# Revit family: Asma klozet için Geberit Duofix elemanı, 112 cm, Alpha 12 cm gömme rezervuar ile, 6_3 litre_PRO_1779723
name_source: partatom
category: Plumbing Fixtures
units: mm (PartAtom-declared; Revit-internal decimal feet)

## family parameters
Always vertical = Yes
Cut with Voids When Loaded = No
OmniClass Number = 23.45.05.00
OmniClass Title = Sanitary Equipment
Part Type = Normal
Room Calculation Point = Yes
Round Connector Dimension = Use Diameter
Shared = No
Work Plane-Based = No

## types (1)
- 458.233.00.2 Asma klozet için Geberit Duofix elemanı, 112 cm, Alpha 12 cm gömme rezervuar ile, 6/3 litre
    ATT_10767 = 0.1 L/s
    Adapter socket = No
    Application purposes = Alçıpan yapılar için
Yarım veya oda yüksekliğinde duvar önü montaj için
Oda yüksekliğinde alçıpanlara montaj için
Bağlantı ölçüleri EN 33:2011 standardına uygun asma klozetler için
62cm’ye kadar projeksiyona sahip asma klozetler için
2 kademeli deşarj için
0–20 cm zemin yapıları için
    Application range = sanitary systems
    Article number key = 458.233.00.2
    BIM Content Version = GEB MG 1.5
    BIM Content revision date = 2024.04.02
    Brand = Geberit
    CW Connection = Yes
    Characteristics = Toz boya kaplı, kendinden destekli çerçeve
Üzeri açık montaj çerçevesi
ø 9 mm delikli çerçeve, ahşap çerçeve yapısına sabitleme için
Üstü açık çerçeveli elemanlara yönelik Geberit Duofix duvar bağlantı için bağlantı delikleri olan çerçeve
Küçük bir temas yüzeyine sahip klozet destekleri için ön hazırlığı yapılmış çerçeve
Galvaniz ayaklar
Ayaklar 0–20 cm aralığında ayarlanabilir
Önden basmalı gömme rezervuar
Yoğuşmaya karşı izolasyonlu gömme rezervuar
Fabrika ayarında hızlı ilave drenaj mümkündür
Su bağlantısı arkada veya üstte ortada
Servis açıklığı şablon kutusu kısaltılabilir
    Connection description 1 = cold water in
    Connection description 2 = sanitary out
    Connection diameter 1 = 15 mm  [stored 0.0492126 ft]
    Connection diameter 2 = 90 mm  [stored 0.295276 ft]
    Connection type at connection 01 = Rp½'' - R½''
    Connection type at connection 02 = DN90/ø90 Spigot
    D = 120 mm  [stored 0.393701 ft]
    D1 = 60 mm  [stored 0.19685 ft]
    Default Elevation = 0 mm  [stored 0 ft]
    Description = Asma klozet için Geberit Duofix elemanı, 112 cm, Alpha 12 cm gömme rezervuar ile, 6/3 litre
    EAN code basic data = 4025410088505
    GEB_culture = tr-TR
    GEB_generic_description = concealed cistern support frame for toilet
    GEB_generic_manufacturer = generic
    GEB_imperial_engineering = No
    GEB_metric_engineering = Yes
    GEB_pimversion = 24.07.12
    GEB_processing_type = T
    GEB_reference = PRO_1779723
    GEB_translations = {"ATT_10673":"EAN code basic data","ATT_10773":"Çalışma basıncı","ATT_10811":"Küçük yıkama miktarı ayar aralığı","ATT_10866":"Yıkama miktarı fabrika ayarı","applicationPurposes":"Application purposes","application_range":"Application range","brandName":"Brand","characteristics":"Characteristics","connection_description1":"Connection description 1","connection_description2":"Connection description 2","GEB_connection_diameter1":"Connection diameter 1","GEB_connection_diameter2":"Connection diameter 2","connection_type_c01":"Connection type at connection 01","connection_type_c02":"Connection type at connection 02","content_creator":"BIM Content creator","content_date_changed":"BIM Content revision date","content_version":"BIM Content Version","key 1000":"Article number key","name":"Name","productBrand":"Product brand","scopeOfDelivery":"Scope of delivery","type":"Type","GEB_cut_length_c01":"Max cutting length at connection 01","angle":"Angle","placement finished floor":"On Finished Floor Level","rod spacing 180mm":"Fastening distance 180mm","rod spacing 230mm":"Fastening distance 230mm","sanitary socket":"Adapter socket","surface height":"Thickness of finished floor","warning":"Warning","fixed_material":"Main material","fixed_material_01":"Main material 01","fixed_material_02":"Main material 02","fixed_material_03":"Main material 03","fixed_material_04":"Main material 04"}
    GEB_use_DN = Yes
    H = 1120 mm  [stored 3.67454 ft]
    H1 = 230 mm  [stored 0.754593 ft]
    H2 = 330 mm
    H3 = 1000 mm  [stored 3.28084 ft]
    HW Connection = No
    IfcDescription = Asma klozet için Geberit Duofix elemanı, 112 cm, Alpha 12 cm gömme rezervuar ile, 6/3 litre
    IfcExportAs = IfcSanitaryTerminal
    IfcExportType = CISTERN
    Küçük yıkama miktarı ayar aralığı = 2-4 l
    LOD300 = No
    LOD400 = Yes
    Main material = Geberit, Plastic, Opaque white
    Main material 01 = Geberit, Steel, Paint Finish, Blue
    Main material 02 = Geberit, Laminate, Ivory, Matte
    Main material 03 = Geberit, Steel, galvanized
    Main material 04 = Geberit, PE-HD, Black
    Manufacturer = Geberit
    Model = Alpha 12 cm
    Name = Asma klozet için Geberit Duofix elemanı, 112 cm, Alpha 12 cm gömme rezervuar ile, 6/3 litre
    Product brand = Duofix
    Scope of delivery = Ara musluk R 1/2", MF uyumlu, adaptör halkalı
Servis açıklığı için şablon kutusu
2 duvar bağlantı
Klozet bağlantı seti, ø 90 mm
Sifon dirseği 90° PE-HD, ø 90 mm
PE-HD geçiş mufu, ø 90 / 110 mm
2 koruyucu tapa
2 dişli rot M12
Sabitleme malzemesi
    Type = Alpha 12 cm
    Vent Connection = No
    W = 500 mm  [stored 1.64042 ft]
    Waste Connection = Yes
    Yıkama miktarı fabrika ayarı = 6 ve 3 l
    cistern_bottom = 530 mm  [stored 1.73885 ft]
    cistern_center = 70 mm  [stored 0.229659 ft]
    cistern_depth = 100 mm  [stored 0.328084 ft]
    cistern_front_offset = 21 mm  [stored 0.0688976 ft]
    cistern_top_offset = 43 mm  [stored 0.141076 ft]
    cistern_width = 420 mm  [stored 1.37795 ft]
    connection_bend = Yes
    frame_btm = 1050 mm  [stored 3.44488 ft]
    outlet_flow = 0.0 L/s
    rod_width_180 = 180 mm  [stored 0.590551 ft]
    rod_width_230 = 230 mm  [stored 0.754593 ft]
    supply_connection_warning = Reducer connected to element not required and should not be accounted for in a BOM
    Çalışma basıncı = 0.1-10 bar

note: [stored X ft] marks values corroborated as IEEE doubles in the binary element streams (Revit-internal decimal feet)

## geometry (parser evidence)
native form markers: Blend x6, Sweep x6
no freeform markers — native parametric forms only
